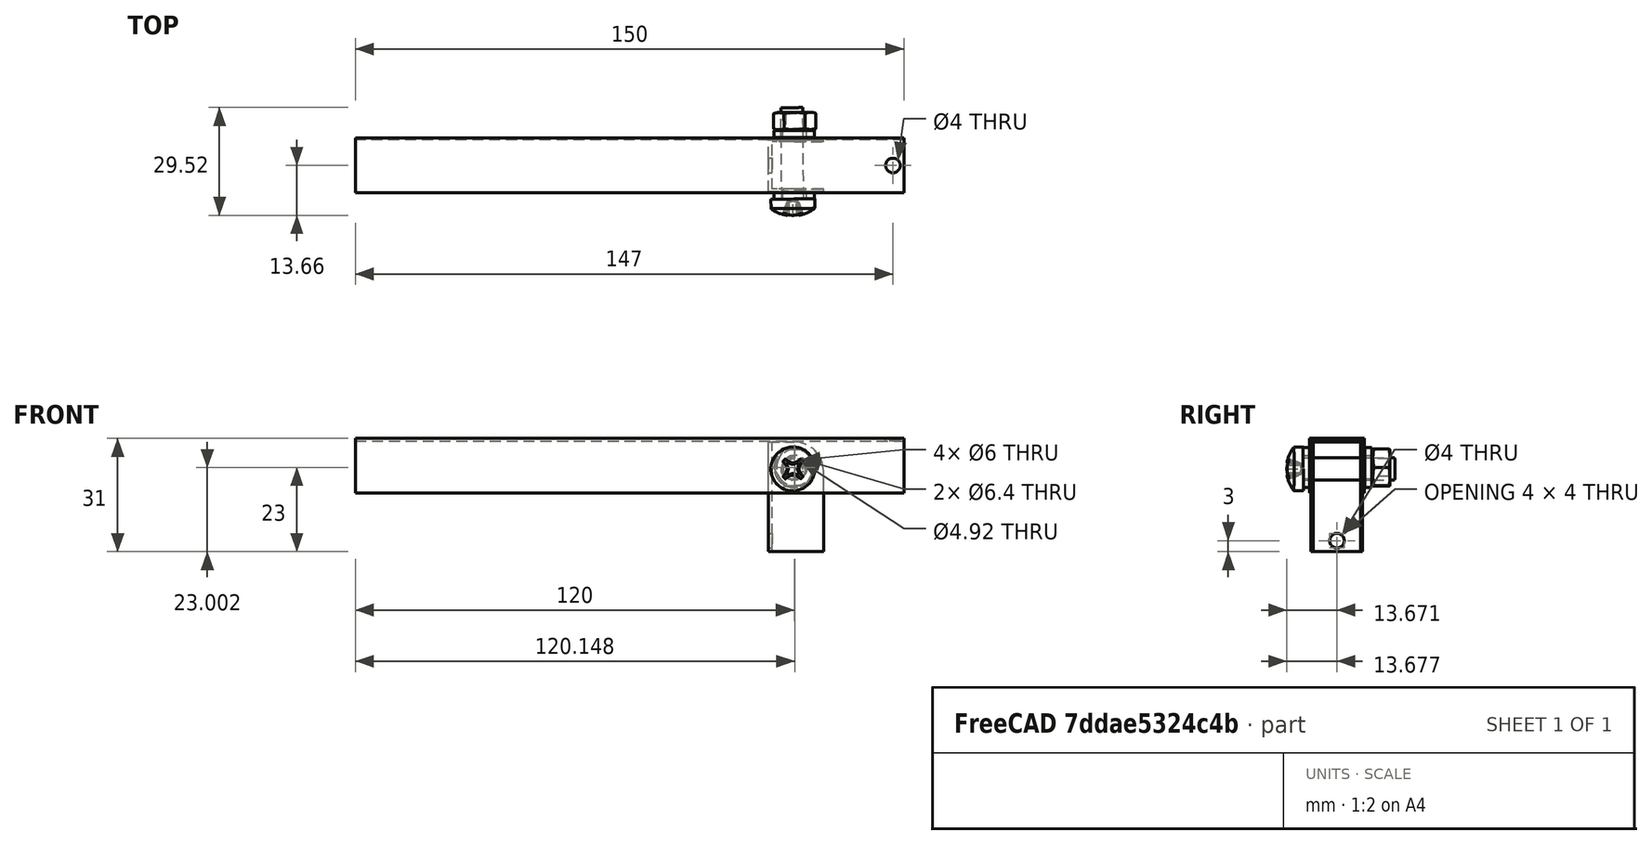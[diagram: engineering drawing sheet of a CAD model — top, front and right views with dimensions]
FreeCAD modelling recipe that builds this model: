
FCSTD DOCUMENT  (FreeCAD 0.15R4671 (Git))
Label: Cutter Lever Hinge Assy3
License: All rights reserved
LicenseURL: http://en.wikipedia.org/wiki/All_rights_reserved
objects: App::DocumentObjectGroupPython×8, Part::Feature×7, Part::FeaturePython×6
note: 13 computed .brp shape members not serialized (recipe doc carries the construction recipe); baked Part::Feature solids carry a one-line shape summary decoded from their .brp

FEATURE [Part::FeaturePython] Washer  label="M6-Washer"  # Fasteners workbench fastener (typed FeaturePython)
  Placement = pos=(120,-2,7) rot=(1,0,0;1.5708rad)
  diameter = 7
  invert = false
  matchOuter = false
  offset = 0
  type = 2
FEATURE [Part::FeaturePython] Cutter_Lever_01  # a2plus imported part (geometry in sourceFile) (typed FeaturePython)
  Placement = pos=(0,-2,0) rot=(0,0,1;0rad)
  fixedPosition = true
  sourceFile = <path> Lever.FCStd
  timeLastImport = 1.53411e+09
  updateColors = true
FEATURE [Part::FeaturePython] Washer001  label="M6-Washer001"  # Fasteners workbench fastener (typed FeaturePython)
  Placement = pos=(120,15,7) rot=(1,0,0;1.5708rad)
  diameter = 7
  invert = false
  matchOuter = false
  offset = 0
  type = 2
FEATURE [Part::FeaturePython] Screw  label="M6x25-Screw"  # Fasteners workbench fastener (typed FeaturePython)
  Placement = pos=(119.623,-3.67426,6.63004) rot=(0.999938,0,0.01111;1.5708rad)
  diameter = 8
  invert = false
  length = 6
  matchOuter = false
  offset = 0
  thread = false
  type = 16
FEATURE [Part::FeaturePython] Nut  label="M6-Nut"  # Fasteners workbench fastener (typed FeaturePython)
  Placement = pos=(120.122,20.0007,7.00136) rot=(0.999938,0,0.01111;1.5708rad)
  diameter = 8
  invert = false
  matchOuter = false
  offset = 0
  thread = false
  type = 1
FEATURE [Part::FeaturePython] Cutter_Lever_Hinge2_01  # a2plus imported part (geometry in sourceFile) (typed FeaturePython)
  Placement = pos=(-1,0,0) rot=(0,0,1;0rad)
  fixedPosition = false
  sourceFile = <path> Lever Hinge2.FCStd
  timeLastImport = 1.53412e+09
  updateColors = true
FEATURE [Part::Feature] trajectory_line
  shape: bbox 2e-07 x 6 x 2e-07 mm, 0 faces, 0 solids (baked)
FEATURE [App::DocumentObjectGroupPython] SimpleGroup  # scripted group (container) (typed FeaturePython)
  AnimationStepTime = 0
  AnimationSteps = 40
  Distance = 6
  Group = -> [trajectory_line]
  Revolutions = 0
FEATURE [Part::Feature] trajectory_line001
  shape: bbox 2e-07 x 6 x 2e-07 mm, 0 faces, 0 solids (baked)
FEATURE [App::DocumentObjectGroupPython] SimpleGroup001  # scripted group (container) (typed FeaturePython)
  AnimationStepTime = 0
  AnimationSteps = 40
  Distance = 6
  Group = -> [trajectory_line001]
  Revolutions = 0
FEATURE [Part::Feature] trajectory_line002
  shape: bbox 0.2222 x 20 x 0.002469 mm, 0 faces, 0 solids (baked)
FEATURE [App::DocumentObjectGroupPython] SimpleGroup002  # scripted group (container) (typed FeaturePython)
  AnimationStepTime = 0
  AnimationSteps = 20
  Distance = 20
  Group = -> [trajectory_line002]
  Revolutions = 0
FEATURE [Part::Feature] trajectory_line003
  shape: bbox 0.2222 x 20 x 0.002469 mm, 0 faces, 0 solids (baked)
FEATURE [App::DocumentObjectGroupPython] SimpleGroup003  # scripted group (container) (typed FeaturePython)
  AnimationStepTime = 0
  AnimationSteps = 20
  Distance = 20
  Group = -> [trajectory_line003]
  Revolutions = 0
FEATURE [Part::Feature] trajectory_line004
  shape: bbox 0.2 x 18 x 0.002222 mm, 0 faces, 0 solids (baked)
FEATURE [App::DocumentObjectGroupPython] SimpleGroup004  # scripted group (container) (typed FeaturePython)
  AnimationStepTime = 0
  AnimationSteps = 30
  Distance = 18
  Group = -> [trajectory_line004]
  Revolutions = 0
FEATURE [Part::Feature] trajectory_line005
  shape: bbox 0.1222 x 11 x 0.001358 mm, 0 faces, 0 solids (baked)
FEATURE [App::DocumentObjectGroupPython] SimpleGroup005  # scripted group (container) (typed FeaturePython)
  AnimationStepTime = 0
  AnimationSteps = 40
  Distance = 11
  Group = -> [trajectory_line005]
  Revolutions = -6
FEATURE [Part::Feature] trajectory_line006
  shape: bbox 2e-07 x 2e-07 x 20 mm, 0 faces, 0 solids (baked)
FEATURE [App::DocumentObjectGroupPython] SimpleGroup006  # scripted group (container) (typed FeaturePython)
  AnimationStepTime = 0
  AnimationSteps = 35
  Distance = 26
  Group = -> [trajectory_line006]
  Revolutions = 0
FEATURE [App::DocumentObjectGroupPython] ExplodedAssembly  # scripted group (container) (typed FeaturePython)
  AnimationStep = 0
  CurrentTrajectory = -1
  Group = -> [SimpleGroup006,SimpleGroup,SimpleGroup001,SimpleGroup002,SimpleGroup003,SimpleGroup004,SimpleGroup005]
  InAnimation = false
  RemoveAllTrajectories = false
  ResetAnimation = false
note: 2 file-system paths scrubbed to <path> (originals preserved in the JSON sidecar)
